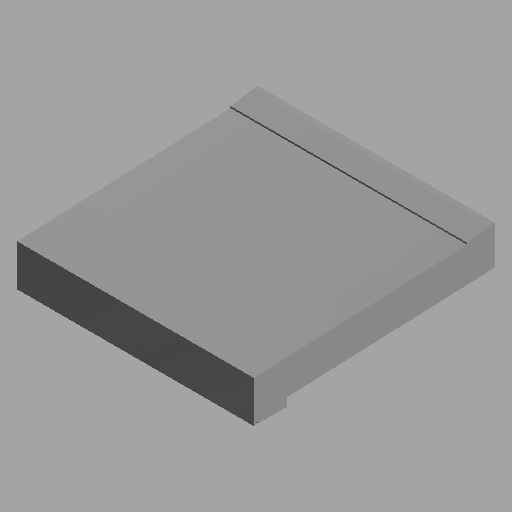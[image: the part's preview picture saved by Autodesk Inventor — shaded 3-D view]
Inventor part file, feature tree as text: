
AUTODESK INVENTOR PART (.ipt)
format: ipt  version: 2023 (Build 270158000, 158)  size: 101,376 bytes
history: native  units: mm (DEFAULTED — no unit token found)
features: extrude x1, sketch x1
ambient origin geometry x8: Origin, YZ Plane, XZ Plane, XY Plane, X Axis, Y Axis, Z Axis, Center Point
bodies: Solid1 (feature_tree), Body1 (feature_tree)
feature tree (2):
  extrude  "Extrusion1"  [1 undecoded]
  sketch  "Sketch2"  dims[d0=0.0mm d1=0.0mm]
note: 1 required parameter value undecoded (feature->parameter linkage not recoverable at this tier; creation-order binding heuristic only, values carry confidence <= 0.55)
